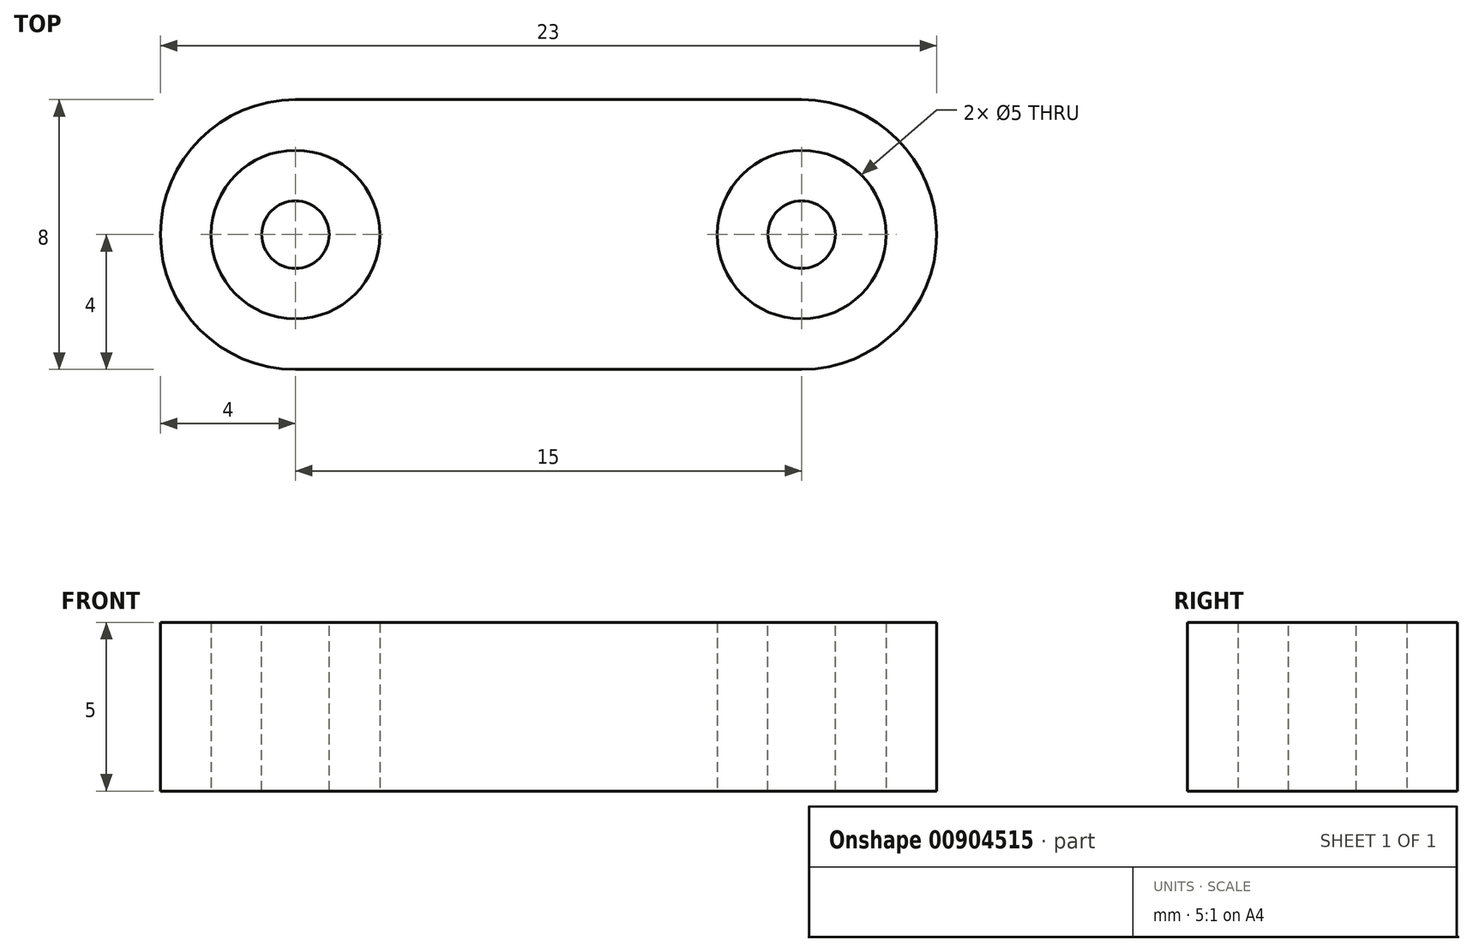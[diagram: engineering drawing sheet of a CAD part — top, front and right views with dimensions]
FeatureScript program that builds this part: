
annotation { "Feature Type Name" : "Feature", "Feature Type Description" : "" }
export const myFeature = defineFeature(function(context is Context, id is Id, definition is map)
    precondition{}
    {
        {
            var Q0;
            Q0=qCreatedBy(makeId("Top.planeOp"),FACE);
            var sketch = newSketch(context, id + "F0", { "sketchPlane" : qUnion([Q0])});
            skCircle(sketch, "E0", {"center": v(0, 0) * mm, "radius": 2.5 * mm});
            skCircle(sketch, "E1", {"center": v(15, 0) * mm, "radius": 2.5 * mm});
            skCircle(sketch, "E2", {"center": v(0, 0) * mm, "radius": 1 * mm});
            skCircle(sketch, "E3", {"center": v(15, 0) * mm, "radius": 1 * mm});
            skArc(sketch, "E4", {"start": v(0, 4) * mm, "mid": v(-4, 0) * mm, "end": v(0, -4) * mm});
            skArc(sketch, "E5", {"start": v(15, -4) * mm, "mid": v(19, 0) * mm, "end": v(15, 4) * mm});
            skLineSegment(sketch, "E6", {"start": v(0, -4) * mm, "end": v(15, -4) * mm});
            skLineSegment(sketch, "E7", {"start": v(0, 4) * mm, "end": v(15, 4) * mm});
            skSolve(sketch);
        }
        {
            var Q0;
            Q0=makeQuery(id+"F0.imprint","IMPRINT",FACE,{"disambiguationData":[TD([[makeQuery(id+"F0.imprint","IMPRINT",EDGE,{"derivedFrom":sQuery(id+"F0.wireOp",EDGE,"E0")}),-1.0]])]});
            extrude(context, id + "F1", {"entities" : qUnion([Q0]), "endBound" : BoundingType.SYMMETRIC, "depth" : 5 * mm, "offsetDistance" : 25.4 * mm});
        }
        {
            var Q0;
            Q0=makeQuery(id+"F1.opExtrude","CAP_FACE",FACE,{"disambiguationData":[OSD([sQuery(id+"F0.wireOp",EDGE,"E0"),sQuery(id+"F0.wireOp",EDGE,"E1"),sQuery(id+"F0.wireOp",EDGE,"E4"),sQuery(id+"F0.wireOp",EDGE,"E5"),sQuery(id+"F0.wireOp",EDGE,"E6"),sQuery(id+"F0.wireOp",EDGE,"E7")])],"isStart":false});
            var sketch = newSketch(context, id + "F2", { "sketchPlane" : qUnion([Q0])});
            skCircle(sketch, "E8", {"center": v(0, 0) * mm, "radius": 1 * mm});
            skCircle(sketch, "E9", {"center": v(15, 0) * mm, "radius": 1 * mm});
            skSolve(sketch);
        }
        {
            var Q0;
            Q0=makeQuery(id+"F2.imprint","IMPRINT",FACE,{"disambiguationData":[TD([[makeQuery(id+"F2.imprint","IMPRINT",EDGE,{"derivedFrom":sQuery(id+"F2.wireOp",EDGE,"E8")}),1.0]])]});
            var Q1;
            Q1=makeQuery(id+"F2.imprint","IMPRINT",FACE,{"disambiguationData":[TD([[makeQuery(id+"F2.imprint","IMPRINT",EDGE,{"derivedFrom":sQuery(id+"F2.wireOp",EDGE,"E9")}),1.0]])]});
            extrude(context, id + "F3", {"entities" : qUnion([Q0, Q1]), "oppositeDirection" : true, "depth" : 5 * mm, "offsetDistance" : 25.4 * mm});
        }
    });
